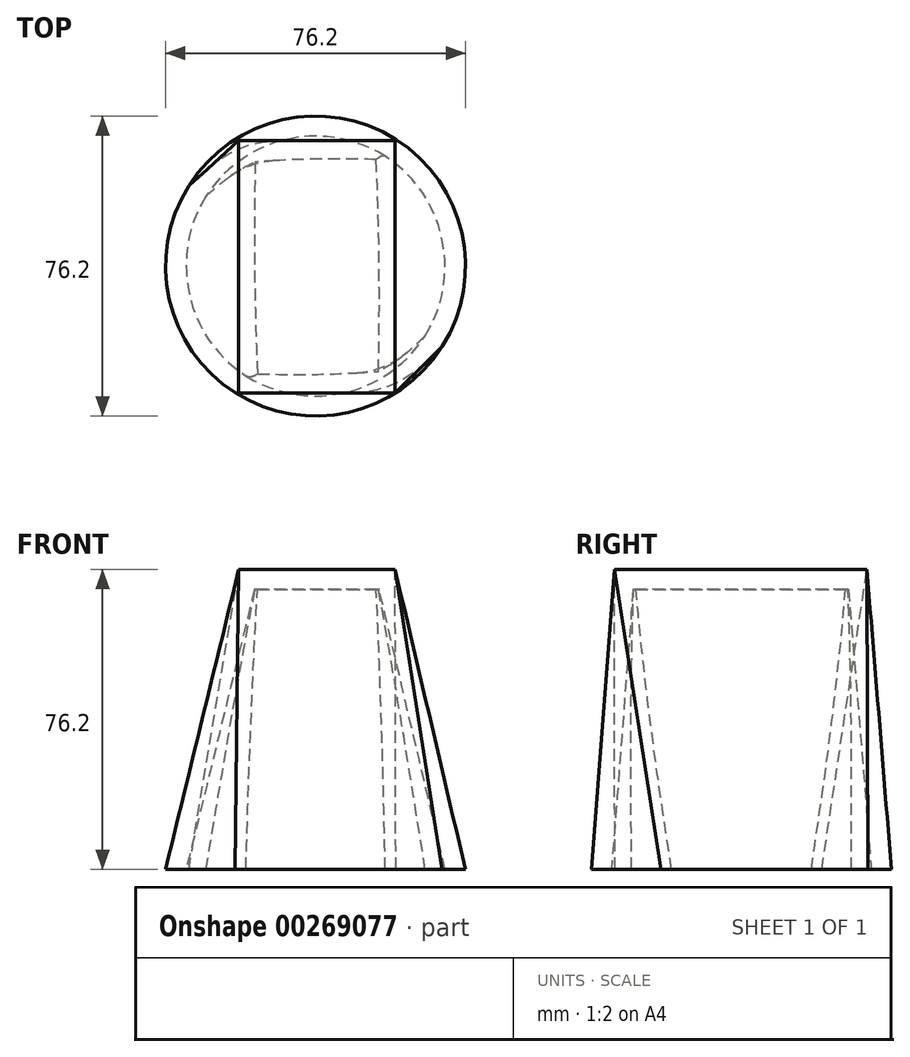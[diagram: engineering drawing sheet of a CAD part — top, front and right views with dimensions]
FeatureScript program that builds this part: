
annotation { "Feature Type Name" : "Feature", "Feature Type Description" : "" }
export const myFeature = defineFeature(function(context is Context, id is Id, definition is map)
    precondition{}
    {
        {
            var Q0;
            Q0=qCreatedBy(makeId("Top.planeOp"),FACE);
            var sketch = newSketch(context, id + "F0", { "sketchPlane" : qUnion([Q0])});
            skCircle(sketch, "E0", {"center": v(0, 0) * mm, "radius": 38.1 * mm});
            skSolve(sketch);
        }
        {
            var Q0;
            Q0=qCreatedBy(makeId("Top.planeOp"),FACE);
            cPlane(context, id + "F1", {"entities" : qUnion([Q0]), "cplaneType" : CPlaneType.OFFSET, "offset" : 76.2 * mm, "width" : 152.4 * mm, "height" : 152.4 * mm});
        }
        {
            var Q0;
            Q0=qCreatedBy(id+"F1.planeOp",FACE);
            var sketch = newSketch(context, id + "F2", { "sketchPlane" : qUnion([Q0])});
            skLineSegment(sketch, "E1.bottom", {"start": v(20.22, 31.9) * mm, "end": v(-19.52, 31.9) * mm});
            skLineSegment(sketch, "E1.top", {"start": v(20.22, -32.25) * mm, "end": v(-19.52, -32.25) * mm});
            skLineSegment(sketch, "E1.left", {"start": v(20.22, 31.9) * mm, "end": v(20.22, -32.25) * mm});
            skLineSegment(sketch, "E1.right", {"start": v(-19.52, 31.9) * mm, "end": v(-19.52, -32.25) * mm});
            skSolve(sketch);
        }
        {
            var Q0;
            Q0=makeQuery(id+"F0.imprint","IMPRINT",FACE,{"disambiguationData":[TD([[makeQuery(id+"F0.imprint","IMPRINT",EDGE,{"derivedFrom":sQuery(id+"F0.wireOp",EDGE,"E0")}),1.0]])]});
            var Q1;
            Q1=makeQuery(id+"F2.imprint","IMPRINT",FACE,{"disambiguationData":[TD([[makeQuery(id+"F2.imprint","IMPRINT",EDGE,{"derivedFrom":sQuery(id+"F2.wireOp",EDGE,"E1.bottom")}),1.0]])]});
            loft(context, id + "F3", {"sheetProfilesArray" : [{ "sheetProfileEntities" : qUnion([Q0]) }, { "sheetProfileEntities" : qUnion([Q1]) }]});
        }
        {
            var Q0;
            Q0=makeQuery(id+"F3.opLoft","CAP_FACE",FACE,{"disambiguationData":[OSD([makeQuery(id+"F0.imprint","IMPRINT",FACE,{"disambiguationData":[TD([[makeQuery(id+"F0.imprint","IMPRINT",EDGE,{"derivedFrom":sQuery(id+"F0.wireOp",EDGE,"E0")}),1.0]])]})])],"isStart":true});
            shell(context, id + "F4", {"entities" : qUnion([Q0]), "thickness" : 5.08 * mm});
        }
    });
